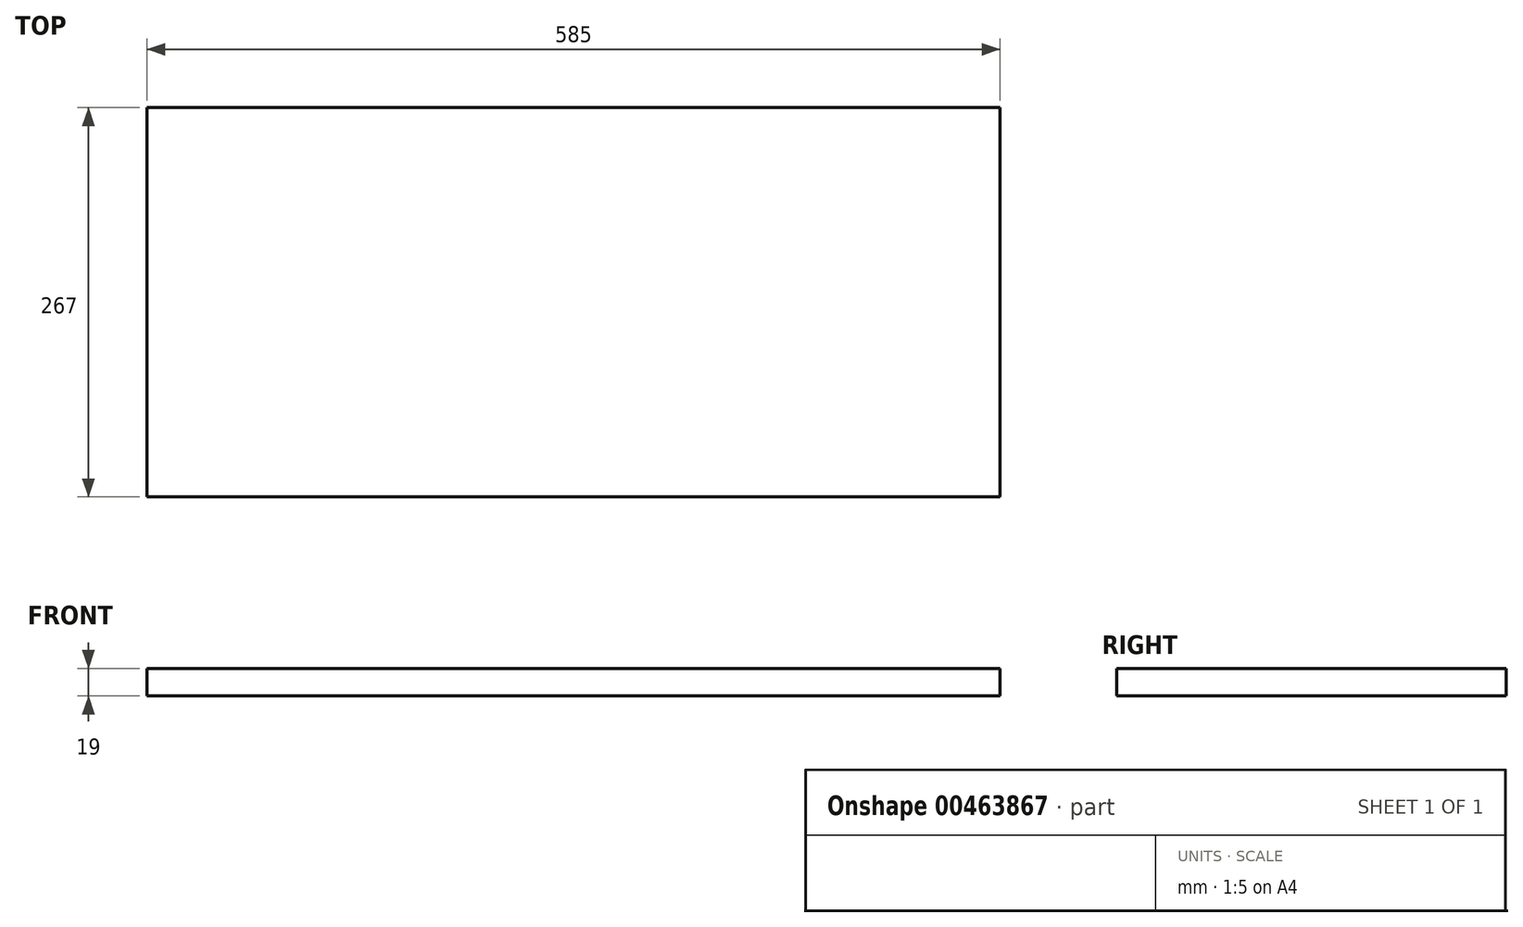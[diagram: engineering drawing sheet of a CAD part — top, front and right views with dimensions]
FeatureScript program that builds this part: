
annotation { "Feature Type Name" : "Feature", "Feature Type Description" : "" }
export const myFeature = defineFeature(function(context is Context, id is Id, definition is map)
    precondition{}
    {
        {
            var Q0;
            Q0=qCreatedBy(makeId("Top.planeOp"),FACE);
            var sketch = newSketch(context, id + "F0", { "sketchPlane" : qUnion([Q0])});
            skLineSegment(sketch, "E0.bottom", {"start": v(0, 0) * mm, "end": v(585, 0) * mm});
            skLineSegment(sketch, "E0.top", {"start": v(0, 267) * mm, "end": v(585, 267) * mm});
            skLineSegment(sketch, "E0.left", {"start": v(0, 0) * mm, "end": v(0, 267) * mm});
            skLineSegment(sketch, "E0.right", {"start": v(585, 0) * mm, "end": v(585, 267) * mm});
            skSolve(sketch);
        }
        {
            var Q0;
            Q0 = qSketchRegion(id + "F0", true);
            extrude(context, id + "F1", {"entities" : qUnion([Q0]), "depth" : 19 * mm});
        }
    });
